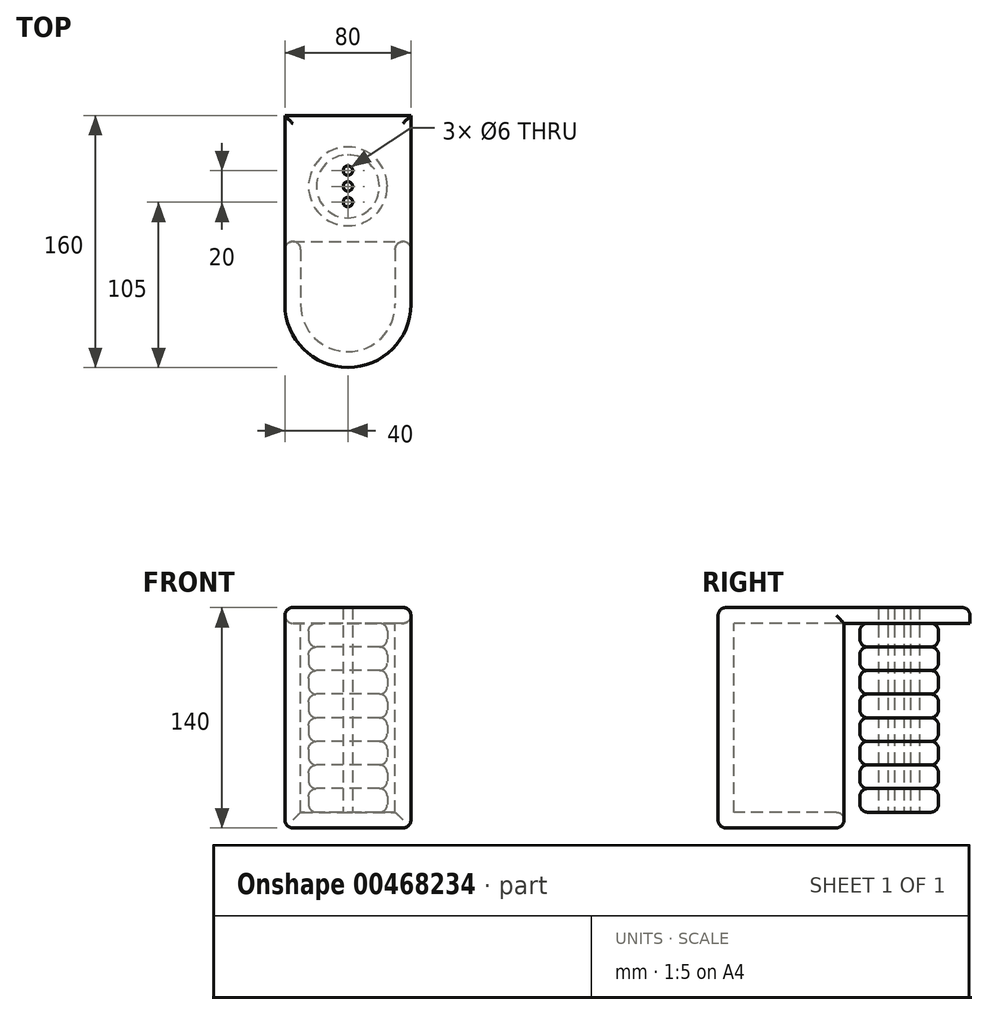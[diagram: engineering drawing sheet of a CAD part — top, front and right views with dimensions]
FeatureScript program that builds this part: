
annotation { "Feature Type Name" : "Feature", "Feature Type Description" : "" }
export const myFeature = defineFeature(function(context is Context, id is Id, definition is map)
    precondition{}
    {
        {
            var Q0;
            Q0=qCreatedBy(makeId("Top.planeOp"),FACE);
            var sketch = newSketch(context, id + "F0", { "sketchPlane" : qUnion([Q0])});
            skCircle(sketch, "E0", {"center": v(0, 0) * mm, "radius": 25 * mm});
            skLineSegment(sketch, "E1", {"start": v(0, 0) * mm, "end": v(0, -10) * mm});
            skLineSegment(sketch, "E2", {"start": v(0, 0) * mm, "end": v(10, 0) * mm});
            skLineSegment(sketch, "E3", {"start": v(0, 0) * mm, "end": v(0, 10) * mm});
            skLineSegment(sketch, "E4", {"start": v(0, 0) * mm, "end": v(-10, 0) * mm});
            skSolve(sketch);
        }
        {
            var Q0;
            Q0=makeQuery(id+"F0.imprint","IMPRINT",FACE,{"disambiguationData":[TD([[makeQuery(id+"F0.imprint","IMPRINT",EDGE,{"derivedFrom":sQuery(id+"F0.wireOp",EDGE,"E0")}),1.0]])]});
            extrude(context, id + "F1", {"entities" : qUnion([Q0]), "depth" : 15 * mm});
        }
        {
            var Q0;
            Q0=makeQuery(id+"F1.opExtrude","CAP_EDGE",EDGE,{"disambiguationData":[OSD([sQuery(id+"F0.wireOp",EDGE,"E0")])],"isStart":true});
            fillet(context, id + "F2", {"entities" : qUnion([Q0]), "radius" : 5 * mm, "tangentPropagation" : true, "allowEdgeOverflow" : false});
        }
        {
            var Q0;
            Q0=makeQuery(id+"F1.opExtrude","CAP_EDGE",EDGE,{"disambiguationData":[OSD([sQuery(id+"F0.wireOp",EDGE,"E0")])],"isStart":false});
            fillet(context, id + "F3", {"entities" : qUnion([Q0]), "radius" : 5 * mm, "tangentPropagation" : true, "allowEdgeOverflow" : false});
        }
        {
            var Q0;
            Q0=makeQuery(id+"F1.opExtrude","CAP_FACE",FACE,{"disambiguationData":[OSD([sQuery(id+"F0.wireOp",EDGE,"E0")])],"isStart":false});
            var sketch = newSketch(context, id + "F4", { "sketchPlane" : qUnion([Q0])});
            skCircle(sketch, "E5", {"center": v(0, 0) * mm, "radius": 25 * mm});
            skSolve(sketch);
        }
        {
            var Q0;
            Q0 = qSketchRegion(id + "F4", true);
            extrude(context, id + "F5", {"entities" : qUnion([Q0]), "operationType" : NewBodyOperationType.ADD, "depth" : 15 * mm});
        }
        {
            var Q0;
            Q0=makeQuery(id+"F5.opExtrude","CAP_EDGE",EDGE,{"disambiguationData":[OSD([sQuery(id+"F4.wireOp",EDGE,"E5")])],"isStart":true});
            var Q1;
            Q1=makeQuery(id+"F5.opExtrude","CAP_EDGE",EDGE,{"disambiguationData":[OSD([sQuery(id+"F4.wireOp",EDGE,"E5")])],"isStart":false});
            fillet(context, id + "F6", {"entities" : qUnion([Q0, Q1]), "radius" : 5 * mm, "tangentPropagation" : true, "allowEdgeOverflow" : false});
        }
        {
            var Q0;
            Q0=makeQuery(id+"F5.opExtrude","CAP_FACE",FACE,{"disambiguationData":[OSD([sQuery(id+"F4.wireOp",EDGE,"E5")])],"isStart":false});
            var sketch = newSketch(context, id + "F7", { "sketchPlane" : qUnion([Q0])});
            skCircle(sketch, "E6", {"center": v(0, 0) * mm, "radius": 25 * mm});
            skSolve(sketch);
        }
        {
            var Q0;
            Q0 = qSketchRegion(id + "F7", true);
            extrude(context, id + "F8", {"entities" : qUnion([Q0]), "operationType" : NewBodyOperationType.ADD, "depth" : 15 * mm});
        }
        {
            var Q0;
            Q0=makeQuery(id+"F8.opExtrude","CAP_EDGE",EDGE,{"disambiguationData":[OSD([sQuery(id+"F7.wireOp",EDGE,"E6")])],"isStart":true});
            var Q1;
            Q1=makeQuery(id+"F8.opExtrude","CAP_EDGE",EDGE,{"disambiguationData":[OSD([sQuery(id+"F7.wireOp",EDGE,"E6")])],"isStart":false});
            fillet(context, id + "F9", {"entities" : qUnion([Q0, Q1]), "radius" : 5 * mm, "tangentPropagation" : true, "allowEdgeOverflow" : false});
        }
        {
            var Q0;
            Q0=makeQuery(id+"F8.opExtrude","CAP_FACE",FACE,{"disambiguationData":[OSD([sQuery(id+"F7.wireOp",EDGE,"E6")])],"isStart":false});
            var sketch = newSketch(context, id + "F10", { "sketchPlane" : qUnion([Q0])});
            skCircle(sketch, "E7", {"center": v(0, 0) * mm, "radius": 25 * mm});
            skSolve(sketch);
        }
        {
            var Q0;
            Q0 = qSketchRegion(id + "F10", true);
            extrude(context, id + "F11", {"entities" : qUnion([Q0]), "operationType" : NewBodyOperationType.ADD, "depth" : 15 * mm});
        }
        {
            var Q0;
            Q0=makeQuery(id+"F11.opExtrude","CAP_EDGE",EDGE,{"disambiguationData":[OSD([sQuery(id+"F10.wireOp",EDGE,"E7")])],"isStart":true});
            var Q1;
            Q1=makeQuery(id+"F11.opExtrude","CAP_EDGE",EDGE,{"disambiguationData":[OSD([sQuery(id+"F10.wireOp",EDGE,"E7")])],"isStart":false});
            fillet(context, id + "F12", {"entities" : qUnion([Q0, Q1]), "radius" : 5 * mm, "tangentPropagation" : true, "allowEdgeOverflow" : false});
        }
        {
            var Q0;
            Q0=makeQuery(id+"F11.opExtrude","CAP_FACE",FACE,{"disambiguationData":[OSD([sQuery(id+"F10.wireOp",EDGE,"E7")])],"isStart":false});
            var sketch = newSketch(context, id + "F13", { "sketchPlane" : qUnion([Q0])});
            skCircle(sketch, "E8", {"center": v(0, 0) * mm, "radius": 25 * mm});
            skSolve(sketch);
        }
        {
            var Q0;
            Q0 = qSketchRegion(id + "F13", true);
            extrude(context, id + "F14", {"entities" : qUnion([Q0]), "operationType" : NewBodyOperationType.ADD, "depth" : 15 * mm});
        }
        {
            var Q0;
            Q0=makeQuery(id+"F14.opExtrude","CAP_EDGE",EDGE,{"disambiguationData":[OSD([sQuery(id+"F13.wireOp",EDGE,"E8")])],"isStart":false});
            var Q1;
            Q1=makeQuery(id+"F14.opExtrude","CAP_EDGE",EDGE,{"disambiguationData":[OSD([sQuery(id+"F13.wireOp",EDGE,"E8")])],"isStart":true});
            fillet(context, id + "F15", {"entities" : qUnion([Q0, Q1]), "radius" : 5 * mm, "tangentPropagation" : true, "allowEdgeOverflow" : false});
        }
        {
            var Q0;
            Q0=makeQuery(id+"F14.opExtrude","CAP_FACE",FACE,{"disambiguationData":[OSD([sQuery(id+"F13.wireOp",EDGE,"E8")])],"isStart":false});
            var sketch = newSketch(context, id + "F16", { "sketchPlane" : qUnion([Q0])});
            skCircle(sketch, "E9", {"center": v(0, 0) * mm, "radius": 25 * mm});
            skSolve(sketch);
        }
        {
            var Q0;
            Q0 = qSketchRegion(id + "F16", true);
            extrude(context, id + "F17", {"entities" : qUnion([Q0]), "operationType" : NewBodyOperationType.ADD, "depth" : 15 * mm});
        }
        {
            var Q0;
            Q0=makeQuery(id+"F17.opExtrude","CAP_EDGE",EDGE,{"disambiguationData":[OSD([sQuery(id+"F16.wireOp",EDGE,"E9")])],"isStart":true});
            var Q1;
            Q1=makeQuery(id+"F17.opExtrude","CAP_EDGE",EDGE,{"disambiguationData":[OSD([sQuery(id+"F16.wireOp",EDGE,"E9")])],"isStart":false});
            fillet(context, id + "F18", {"entities" : qUnion([Q0, Q1]), "radius" : 5 * mm, "tangentPropagation" : true, "allowEdgeOverflow" : false});
        }
        {
            var Q0;
            Q0=makeQuery(id+"F17.opExtrude","CAP_FACE",FACE,{"disambiguationData":[OSD([sQuery(id+"F16.wireOp",EDGE,"E9")])],"isStart":false});
            var sketch = newSketch(context, id + "F19", { "sketchPlane" : qUnion([Q0])});
            skCircle(sketch, "E10", {"center": v(0, 0) * mm, "radius": 25 * mm});
            skSolve(sketch);
        }
        {
            var Q0;
            Q0 = qSketchRegion(id + "F19", true);
            extrude(context, id + "F20", {"entities" : qUnion([Q0]), "operationType" : NewBodyOperationType.ADD, "depth" : 15 * mm});
        }
        {
            var Q0;
            Q0=makeQuery(id+"F20.opExtrude","CAP_EDGE",EDGE,{"disambiguationData":[OSD([sQuery(id+"F19.wireOp",EDGE,"E10")])],"isStart":false});
            var Q1;
            Q1=makeQuery(id+"F20.opExtrude","CAP_EDGE",EDGE,{"disambiguationData":[OSD([sQuery(id+"F19.wireOp",EDGE,"E10")])],"isStart":true});
            fillet(context, id + "F21", {"entities" : qUnion([Q0, Q1]), "radius" : 5 * mm, "tangentPropagation" : true, "allowEdgeOverflow" : false});
        }
        {
            var Q0;
            Q0=makeQuery(id+"F20.opExtrude","CAP_FACE",FACE,{"disambiguationData":[OSD([sQuery(id+"F19.wireOp",EDGE,"E10")])],"isStart":false});
            var sketch = newSketch(context, id + "F22", { "sketchPlane" : qUnion([Q0])});
            skCircle(sketch, "E11", {"center": v(0, 0) * mm, "radius": 25 * mm});
            skSolve(sketch);
        }
        {
            var Q0;
            Q0 = qSketchRegion(id + "F22", true);
            extrude(context, id + "F23", {"entities" : qUnion([Q0]), "operationType" : NewBodyOperationType.ADD, "depth" : 15 * mm});
        }
        {
            var Q0;
            Q0=makeQuery(id+"F23.opExtrude","CAP_EDGE",EDGE,{"disambiguationData":[OSD([sQuery(id+"F22.wireOp",EDGE,"E11")])],"isStart":false});
            var Q1;
            Q1=makeQuery(id+"F23.opExtrude","CAP_EDGE",EDGE,{"disambiguationData":[OSD([sQuery(id+"F22.wireOp",EDGE,"E11")])],"isStart":true});
            fillet(context, id + "F24", {"entities" : qUnion([Q0, Q1]), "radius" : 5 * mm, "tangentPropagation" : true, "allowEdgeOverflow" : false});
        }
        {
            var Q0;
            Q0=makeQuery(id+"F23.opExtrude","CAP_FACE",FACE,{"disambiguationData":[OSD([sQuery(id+"F22.wireOp",EDGE,"E11")])],"isStart":false});
            var sketch = newSketch(context, id + "F25", { "sketchPlane" : qUnion([Q0])});
            skLineSegment(sketch, "E12.bottom", {"start": v(-40, 75) * mm, "end": v(40, 75) * mm});
            skLineSegment(sketch, "E12.top", {"start": v(-40, -75) * mm, "end": v(40, -75) * mm});
            skLineSegment(sketch, "E12.left", {"start": v(-40, 75) * mm, "end": v(-40, -75) * mm});
            skLineSegment(sketch, "E12.right", {"start": v(40, 75) * mm, "end": v(40, -75) * mm});
            skPoint(sketch, "E12.middle", {"position": v(0, 0) * mm});
            skSolve(sketch);
        }
        {
            var Q0;
            Q0 = qSketchRegion(id + "F25", true);
            extrude(context, id + "F26", {"entities" : qUnion([Q0]), "operationType" : NewBodyOperationType.ADD, "depth" : 10 * mm});
        }
        {
            var Q0;
            Q0=makeQuery(id+"F26.opExtrude","SWEPT_FACE",FACE,{"disambiguationData":[OSD([sQuery(id+"F25.wireOp",EDGE,"E12.bottom")])]});
            extrude(context, id + "F27", {"entities" : qUnion([Q0]), "operationType" : NewBodyOperationType.REMOVE, "oppositeDirection" : true, "depth" : 30 * mm});
        }
        {
            var Q0;
            Q0=makeQuery(id+"F26.opExtrude","SWEPT_FACE",FACE,{"disambiguationData":[OSD([sQuery(id+"F25.wireOp",EDGE,"E12.top")])]});
            extrude(context, id + "F28", {"entities" : qUnion([Q0]), "operationType" : NewBodyOperationType.ADD, "depth" : 40 * mm});
        }
        {
            var Q0;
            {var subQ0=sQuery(id+"F25.wireOp",EDGE,"E12.top");Q0=makeQuery(id+"F28.boolean.opBoolean","MERGE",FACE,{"derivedFrom":[makeQuery(id+"F26.opExtrude","CAP_FACE",FACE,{"disambiguationData":[OSD([sQuery(id+"F25.wireOp",EDGE,"E12.bottom"),subQ0,sQuery(id+"F25.wireOp",EDGE,"E12.left"),sQuery(id+"F25.wireOp",EDGE,"E12.right")])],"isStart":true}),makeQuery(id+"F28.opExtrude","SWEPT_FACE",FACE,{"disambiguationData":[OSD([subQ0]),TDD([makeQuery(id+"F26.opExtrude","CAP_EDGE",EDGE,{"disambiguationData":[OSD([subQ0])],"isStart":true})])]})]});}
            var sketch = newSketch(context, id + "F29", { "sketchPlane" : qUnion([Q0])});
            skLineSegment(sketch, "E13", {"start": v(40, 115) * mm, "end": v(40, 75) * mm});
            skArc(sketch, "E14", {"start": v(40, 75) * mm, "mid": v(0, 115) * mm, "end": v(-40, 75) * mm});
            skLineSegment(sketch, "E15", {"start": v(40, 75) * mm, "end": v(30, 75) * mm});
            skLineSegment(sketch, "E16", {"start": v(-40, 75) * mm, "end": v(-30, 75) * mm});
            skLineSegment(sketch, "E17", {"start": v(0, 115) * mm, "end": v(0, 105) * mm});
            skPoint(sketch, "E17.endSnap0", {"position": v(0, 115) * mm});
            skArc(sketch, "E18", {"start": v(30, 75) * mm, "mid": v(0, 105) * mm, "end": v(-30, 75) * mm});
            skSolve(sketch);
        }
        {
            var Q0;
            Q0 = qSketchRegion(id + "F29", true);
            extrude(context, id + "F30", {"entities" : qUnion([Q0]), "operationType" : NewBodyOperationType.ADD, "depth" : 120 * mm});
        }
        {
            var Q0;
            {var subQ0=sQuery(id+"F25.wireOp",EDGE,"E12.right");var subQ1=sQuery(id+"F25.wireOp",EDGE,"E12.top");var subQ2=makeQuery(id+"F28.opExtrude","SWEPT_FACE",FACE,{"disambiguationData":[OSD([subQ1]),TDD([makeQuery(id+"F26.opExtrude","CAP_EDGE",EDGE,{"disambiguationData":[OSD([subQ1])],"isStart":true})])]});var subQ3=makeQuery(id+"F26.opExtrude","CAP_FACE",FACE,{"disambiguationData":[OSD([sQuery(id+"F25.wireOp",EDGE,"E12.bottom"),subQ1,sQuery(id+"F25.wireOp",EDGE,"E12.left"),subQ0])],"isStart":true});Q0=makeQuery(id+"F30.boolean.opBoolean","SPLIT",FACE,{"disambiguationData":[TD([subQ3,makeQuery(id+"F26.opExtrude","SWEPT_FACE",FACE,{"disambiguationData":[OSD([subQ0])]}),makeQuery(id+"F28.opExtrude","SWEPT_FACE",FACE,{"disambiguationData":[OSD([subQ1,subQ0])]}),subQ2,makeQuery(id+"F28.opExtrude","CAP_FACE",FACE,{"disambiguationData":[OSD([subQ1])],"isStart":false}),makeQuery(id+"F30.opExtrude","SWEPT_FACE",FACE,{"disambiguationData":[OSD([sQuery(id+"F29.wireOp",EDGE,"E14")])]}),makeQuery(id+"F30.opExtrude","SWEPT_FACE",FACE,{"disambiguationData":[OSD([sQuery(id+"F29.wireOp",EDGE,"E15")])]})])],"derivedFrom":makeQuery(id+"F28.boolean.opBoolean","MERGE",FACE,{"derivedFrom":[subQ3,subQ2]})});}
            var Q1;
            {var subQ0=sQuery(id+"F25.wireOp",EDGE,"E12.left");var subQ1=sQuery(id+"F25.wireOp",EDGE,"E12.top");var subQ2=makeQuery(id+"F28.opExtrude","SWEPT_FACE",FACE,{"disambiguationData":[OSD([subQ1]),TDD([makeQuery(id+"F26.opExtrude","CAP_EDGE",EDGE,{"disambiguationData":[OSD([subQ1])],"isStart":true})])]});var subQ3=makeQuery(id+"F26.opExtrude","CAP_FACE",FACE,{"disambiguationData":[OSD([sQuery(id+"F25.wireOp",EDGE,"E12.bottom"),subQ1,subQ0,sQuery(id+"F25.wireOp",EDGE,"E12.right")])],"isStart":true});Q1=makeQuery(id+"F30.boolean.opBoolean","SPLIT",FACE,{"disambiguationData":[TD([subQ3,makeQuery(id+"F26.opExtrude","SWEPT_FACE",FACE,{"disambiguationData":[OSD([subQ0])]}),makeQuery(id+"F28.opExtrude","SWEPT_FACE",FACE,{"disambiguationData":[OSD([subQ1,subQ0])]}),subQ2,makeQuery(id+"F28.opExtrude","CAP_FACE",FACE,{"disambiguationData":[OSD([subQ1])],"isStart":false}),makeQuery(id+"F30.opExtrude","SWEPT_FACE",FACE,{"disambiguationData":[OSD([sQuery(id+"F29.wireOp",EDGE,"E14")])]}),makeQuery(id+"F30.opExtrude","SWEPT_FACE",FACE,{"disambiguationData":[OSD([sQuery(id+"F29.wireOp",EDGE,"E16")])]})])],"derivedFrom":makeQuery(id+"F28.boolean.opBoolean","MERGE",FACE,{"derivedFrom":[subQ3,subQ2]})});}
            extrude(context, id + "F31", {"entities" : qUnion([Q0, Q1]), "operationType" : NewBodyOperationType.REMOVE, "oppositeDirection" : true, "depth" : 25 * mm});
        }
        {
            var Q0;
            Q0=makeQuery(id+"F30.opExtrude","SWEPT_FACE",FACE,{"disambiguationData":[OSD([sQuery(id+"F29.wireOp",EDGE,"E16")])]});
            var Q1;
            Q1=makeQuery(id+"F30.opExtrude","SWEPT_FACE",FACE,{"disambiguationData":[OSD([sQuery(id+"F29.wireOp",EDGE,"E15")])]});
            extrude(context, id + "F32", {"entities" : qUnion([Q0, Q1]), "operationType" : NewBodyOperationType.ADD, "depth" : 40 * mm});
        }
        {
            var Q0;
            {var subQ0=sQuery(id+"F29.wireOp",EDGE,"E16");var subQ1=sQuery(id+"F29.wireOp",EDGE,"E15");Q0=makeQuery(id+"F32.boolean.opBoolean","MERGE",FACE,{"derivedFrom":[makeQuery(id+"F30.opExtrude","CAP_FACE",FACE,{"disambiguationData":[OSD([sQuery(id+"F29.wireOp",EDGE,"E14"),subQ1,subQ0,sQuery(id+"F29.wireOp",EDGE,"E18")])],"isStart":false}),makeQuery(id+"F32.opExtrude","SWEPT_FACE",FACE,{"disambiguationData":[OSD([subQ1]),TDD([makeQuery(id+"F30.opExtrude","CAP_EDGE",EDGE,{"disambiguationData":[OSD([subQ1])],"isStart":false})])]}),makeQuery(id+"F32.opExtrude","SWEPT_FACE",FACE,{"disambiguationData":[OSD([subQ0]),TDD([makeQuery(id+"F30.opExtrude","CAP_EDGE",EDGE,{"disambiguationData":[OSD([subQ0])],"isStart":false})])]})]});}
            var sketch = newSketch(context, id + "F33", { "sketchPlane" : qUnion([Q0])});
            skLineSegment(sketch, "E19", {"start": v(-40, 35) * mm, "end": v(40, 35) * mm});
            skLineSegment(sketch, "E20", {"start": v(40, 35) * mm, "end": v(40, 75) * mm});
            skLineSegment(sketch, "E21", {"start": v(-40, 35) * mm, "end": v(-40, 75) * mm});
            skArc(sketch, "E22", {"start": v(40, 75) * mm, "mid": v(0, 115) * mm, "end": v(-40, 75) * mm});
            skSolve(sketch);
        }
        {
            var Q0;
            Q0 = qSketchRegion(id + "F33", true);
            extrude(context, id + "F34", {"entities" : qUnion([Q0]), "operationType" : NewBodyOperationType.ADD, "depth" : 10 * mm});
        }
        {
            var Q0;
            Q0=makeQuery(id+"F34.opExtrude","CAP_EDGE",EDGE,{"disambiguationData":[OSD([sQuery(id+"F33.wireOp",EDGE,"E20")])],"isStart":false});
            var Q1;
            Q1=makeQuery(id+"F34.opExtrude","CAP_FACE",FACE,{"disambiguationData":[OSD([sQuery(id+"F33.wireOp",EDGE,"E19"),sQuery(id+"F33.wireOp",EDGE,"E20"),sQuery(id+"F33.wireOp",EDGE,"E21"),sQuery(id+"F33.wireOp",EDGE,"E22")])],"isStart":false});
            fillet(context, id + "F35", {"entities" : qUnion([Q0, Q1]), "radius" : 5 * mm, "tangentPropagation" : true, "allowEdgeOverflow" : false});
        }
        {
            var Q0;
            Q0=makeQuery(id+"F34.boolean.opBoolean","MERGE",EDGE,{"derivedFrom":[makeQuery(id+"F32.opExtrude","CAP_EDGE",EDGE,{"disambiguationData":[OSD([sQuery(id+"F25.wireOp",EDGE,"E12.top"),sQuery(id+"F25.wireOp",EDGE,"E12.right"),sQuery(id+"F29.wireOp",EDGE,"E13"),sQuery(id+"F29.wireOp",EDGE,"E14"),sQuery(id+"F29.wireOp",EDGE,"E15")])],"isStart":false}),makeQuery(id+"F34.opExtrude","SWEPT_EDGE",EDGE,{"disambiguationData":[OSD([sQuery(id+"F33.wireOp",EDGE,"E19"),sQuery(id+"F33.wireOp",EDGE,"E20")])]})]});
            var Q1;
            Q1=makeQuery(id+"F34.boolean.opBoolean","MERGE",EDGE,{"derivedFrom":[makeQuery(id+"F32.opExtrude","CAP_EDGE",EDGE,{"disambiguationData":[OSD([sQuery(id+"F25.wireOp",EDGE,"E12.top"),sQuery(id+"F25.wireOp",EDGE,"E12.left"),sQuery(id+"F29.wireOp",EDGE,"E14"),sQuery(id+"F29.wireOp",EDGE,"E16")])],"isStart":false}),makeQuery(id+"F34.opExtrude","SWEPT_EDGE",EDGE,{"disambiguationData":[OSD([sQuery(id+"F33.wireOp",EDGE,"E19"),sQuery(id+"F33.wireOp",EDGE,"E21")])]})]});
            var Q2;
            Q2=makeQuery(id+"F32.opExtrude","CAP_EDGE",EDGE,{"disambiguationData":[OSD([sQuery(id+"F29.wireOp",EDGE,"E16"),sQuery(id+"F29.wireOp",EDGE,"E18")])],"isStart":false});
            var Q3;
            Q3=makeQuery(id+"F32.opExtrude","CAP_EDGE",EDGE,{"disambiguationData":[OSD([sQuery(id+"F29.wireOp",EDGE,"E15"),sQuery(id+"F29.wireOp",EDGE,"E18")])],"isStart":false});
            fillet(context, id + "F36", {"entities" : qUnion([Q0, Q1, Q2, Q3]), "radius" : 5 * mm, "tangentPropagation" : true, "allowEdgeOverflow" : false});
        }
        {
            var Q0;
            Q0=makeQuery(id+"F34.opExtrude","CAP_EDGE",EDGE,{"disambiguationData":[OSD([sQuery(id+"F33.wireOp",EDGE,"E19")])],"isStart":true});
            fillet(context, id + "F37", {"entities" : qUnion([Q0]), "radius" : 5 * mm, "tangentPropagation" : true, "allowEdgeOverflow" : false});
        }
        {
            var Q0;
            Q0=makeQuery(id+"F27.boolean.opBoolean","COPY",EDGE,{"derivedFrom":makeQuery(id+"F27.opExtrude","CAP_EDGE",EDGE,{"disambiguationData":[OSD([sQuery(id+"F25.wireOp",EDGE,"E12.bottom"),sQuery(id+"F25.wireOp",EDGE,"E12.right")])],"isStart":false})});
            var Q1;
            Q1=makeQuery(id+"F27.boolean.opBoolean","COPY",EDGE,{"derivedFrom":makeQuery(id+"F27.opExtrude","CAP_EDGE",EDGE,{"disambiguationData":[OSD([sQuery(id+"F25.wireOp",EDGE,"E12.bottom"),sQuery(id+"F25.wireOp",EDGE,"E12.left")])],"isStart":false})});
            var Q2;
            {var subQ0=sQuery(id+"F25.wireOp",EDGE,"E12.top");Q2=makeQuery(id+"F28.boolean.opBoolean","MERGE",FACE,{"derivedFrom":[makeQuery(id+"F26.opExtrude","CAP_FACE",FACE,{"disambiguationData":[OSD([sQuery(id+"F25.wireOp",EDGE,"E12.bottom"),subQ0,sQuery(id+"F25.wireOp",EDGE,"E12.left"),sQuery(id+"F25.wireOp",EDGE,"E12.right")])],"isStart":false}),makeQuery(id+"F28.opExtrude","SWEPT_FACE",FACE,{"disambiguationData":[OSD([subQ0]),TDD([makeQuery(id+"F26.opExtrude","CAP_EDGE",EDGE,{"disambiguationData":[OSD([subQ0])],"isStart":false})])]})]});}
            var Q3;
            {var subQ0=sQuery(id+"F25.wireOp",EDGE,"E12.bottom");Q3=makeQuery(id+"F27.boolean.opBoolean","COPY",EDGE,{"derivedFrom":makeQuery(id+"F27.opExtrude","CAP_EDGE",EDGE,{"disambiguationData":[OSD([subQ0]),TDD([makeQuery(id+"F26.opExtrude","CAP_EDGE",EDGE,{"disambiguationData":[OSD([subQ0])],"isStart":true})])],"isStart":false})});}
            var Q4;
            {var subQ0=sQuery(id+"F25.wireOp",EDGE,"E12.bottom");var subQ1=sQuery(id+"F25.wireOp",EDGE,"E12.left");var subQ2=sQuery(id+"F25.wireOp",EDGE,"E12.top");Q4=makeQuery(id+"F30.boolean.opBoolean","SPLIT",EDGE,{"disambiguationData":[TD([makeQuery(id+"F27.boolean.opBoolean","COPY",FACE,{"derivedFrom":makeQuery(id+"F27.opExtrude","CAP_FACE",FACE,{"disambiguationData":[OSD([subQ0])],"isStart":false})})])],"derivedFrom":makeQuery(id+"F28.boolean.opBoolean","MERGE",EDGE,{"derivedFrom":[makeQuery(id+"F26.opExtrude","CAP_EDGE",EDGE,{"disambiguationData":[OSD([subQ1])],"isStart":true}),makeQuery(id+"F28.opExtrude","SWEPT_EDGE",EDGE,{"disambiguationData":[OSD([subQ2,subQ1]),TDD([makeQuery(id+"F26.opExtrude","CAP_VERTEX",VERTEX,{"disambiguationData":[OSD([subQ2,subQ1])],"isStart":true})])]})]})});}
            var Q5;
            {var subQ0=sQuery(id+"F25.wireOp",EDGE,"E12.bottom");var subQ1=sQuery(id+"F25.wireOp",EDGE,"E12.right");var subQ2=sQuery(id+"F25.wireOp",EDGE,"E12.top");Q5=makeQuery(id+"F30.boolean.opBoolean","SPLIT",EDGE,{"disambiguationData":[TD([makeQuery(id+"F27.boolean.opBoolean","COPY",FACE,{"derivedFrom":makeQuery(id+"F27.opExtrude","CAP_FACE",FACE,{"disambiguationData":[OSD([subQ0])],"isStart":false})})])],"derivedFrom":makeQuery(id+"F28.boolean.opBoolean","MERGE",EDGE,{"derivedFrom":[makeQuery(id+"F26.opExtrude","CAP_EDGE",EDGE,{"disambiguationData":[OSD([subQ1])],"isStart":true}),makeQuery(id+"F28.opExtrude","SWEPT_EDGE",EDGE,{"disambiguationData":[OSD([subQ2,subQ1]),TDD([makeQuery(id+"F26.opExtrude","CAP_VERTEX",VERTEX,{"disambiguationData":[OSD([subQ2,subQ1])],"isStart":true})])]})]})});}
            fillet(context, id + "F38", {"entities" : qUnion([Q0, Q1, Q2, Q3, Q4, Q5]), "radius" : 5 * mm, "tangentPropagation" : true, "allowEdgeOverflow" : false});
        }
        {
            var Q0;
            Q0=sQuery(id+"F0.wireOp",VERTEX,"E0.center");
            var Q1;
            Q1=sQuery(id+"F0.wireOp",VERTEX,"E3.end");
            var Q2;
            Q2=sQuery(id+"F0.wireOp",VERTEX,"E1.end");
            var Q3;
            Q3=makeQuery(id+"F1.opExtrude","SWEPT_BODY",BODY,{"disambiguationData":[OSD([sQuery(id+"F0.wireOp",EDGE,"E0")])]});
            hole(context, id + "F39", {"style" : HoleStyle.SIMPLE, "endStyle" : HoleEndStyle.BLIND, "oppositeDirection" : true, "holeDiameter" : 6 * mm, "holeDepth" : 140 * mm, "isTappedThrough" : true, "tappedDepth" : 12 * mm, "tapClearance" : 3, "locations" : qUnion([Q0, Q1, Q2]), "scope" : qUnion([Q3])});
        }
    });
